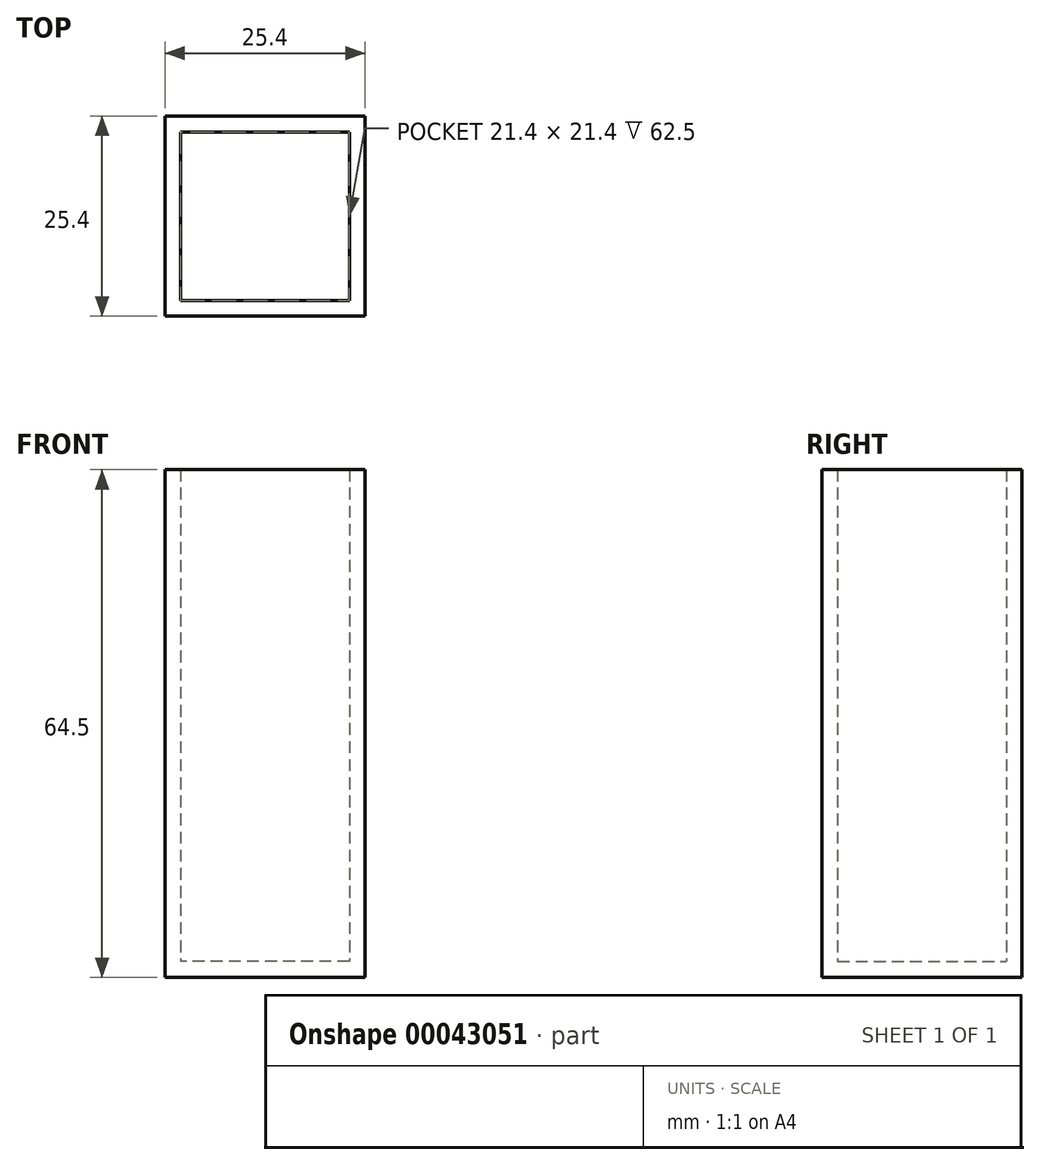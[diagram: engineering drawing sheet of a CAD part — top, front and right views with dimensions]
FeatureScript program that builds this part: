
annotation { "Feature Type Name" : "Feature", "Feature Type Description" : "" }
export const myFeature = defineFeature(function(context is Context, id is Id, definition is map)
    precondition{}
    {
        {
            var Q0;
            Q0=qCreatedBy(makeId("Top.planeOp"),FACE);
            var sketch = newSketch(context, id + "F0", { "sketchPlane" : qUnion([Q0])});
            skLineSegment(sketch, "E0.rect.bottom", {"start": v(12.7, -12.7) * mm, "end": v(-12.7, -12.7) * mm});
            skLineSegment(sketch, "E0.rect.top", {"start": v(12.7, 12.7) * mm, "end": v(-12.7, 12.7) * mm});
            skLineSegment(sketch, "E0.rect.left", {"start": v(12.7, -12.7) * mm, "end": v(12.7, 12.7) * mm});
            skLineSegment(sketch, "E0.rect.right", {"start": v(-12.7, -12.7) * mm, "end": v(-12.7, 12.7) * mm});
            skPoint(sketch, "E0.rect.middle", {"position": v(0, 0) * mm});
            skLineSegment(sketch, "E1.0", {"start": v(10.7, -10.7) * mm, "end": v(10.7, 10.7) * mm});
            skLineSegment(sketch, "E1.1", {"start": v(10.7, -10.7) * mm, "end": v(-10.7, -10.7) * mm});
            skLineSegment(sketch, "E1.2", {"start": v(-10.7, -10.7) * mm, "end": v(-10.7, 10.7) * mm});
            skLineSegment(sketch, "E1.3", {"start": v(10.7, 10.7) * mm, "end": v(-10.7, 10.7) * mm});
            skSolve(sketch);
        }
        {
            var Q0;
            Q0=makeQuery(id+"F0.imprint","IMPRINT",FACE,{"disambiguationData":[TD([[makeQuery(id+"F0.imprint","IMPRINT",EDGE,{"derivedFrom":sQuery(id+"F0.wireOp",EDGE,"E0.rect.bottom")}),-1.0]])]});
            extrude(context, id + "F1", {"entities" : qUnion([Q0]), "depth" : (125 / 2) * mm});
        }
        {
            var Q0;
            Q0=makeQuery(id+"F0.imprint","IMPRINT",FACE,{"disambiguationData":[TD([[makeQuery(id+"F0.imprint","IMPRINT",EDGE,{"derivedFrom":sQuery(id+"F0.wireOp",EDGE,"E1.0")}),1.0]])]});
            var Q1;
            Q1=makeQuery(id+"F0.imprint","IMPRINT",FACE,{"disambiguationData":[TD([[makeQuery(id+"F0.imprint","IMPRINT",EDGE,{"derivedFrom":sQuery(id+"F0.wireOp",EDGE,"E0.rect.bottom")}),-1.0]])]});
            extrude(context, id + "F2", {"entities" : qUnion([Q0, Q1]), "operationType" : NewBodyOperationType.ADD, "oppositeDirection" : true, "depth" : 2 * mm});
        }
    });
